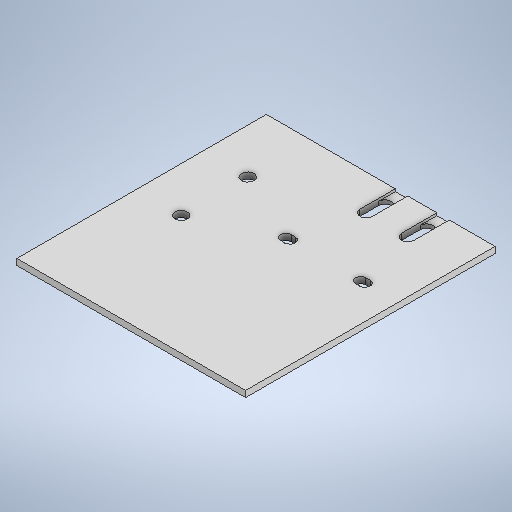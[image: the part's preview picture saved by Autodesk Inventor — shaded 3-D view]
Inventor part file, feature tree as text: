
AUTODESK INVENTOR PART (.ipt)
format: ipt  version: 2025.2 (Build 292293000, 293)  size: 290,816 bytes
history: native  units: mm
features: extrude x5, sketch x4
ambient origin geometry x8: Origin, YZ Plane, XZ Plane, XY Plane, X Axis, Y Axis, Z Axis, Center Point
bodies: Solid1 (feature_tree)
feature tree (9):
  extrude  "Extrusion1"  Depth=120.0mm
  sketch  "Sketch4"  dims[d2=3.0mm d3=0.0mm d14=20.0mm]
  extrude  "Extrusion3"  Depth=20.0mm
  extrude  "Extrusion5"  Depth=6.0mm
  extrude  "Extrusion6"  Depth=5.0mm
  extrude  "Extrusion7"  Depth=5.0mm
  sketch  "Sketch1"  dims[d0=150.0mm d1=120.0mm]
  sketch  "Sketch6"  dims[d15=20.0mm d16=6.0mm]
  sketch  "Sketch7"  dims[d17=6.0mm d18=5.0mm d19=5.0mm d20=3.0mm d21=3.0mm d22=3.0mm d23=3.0mm d24=0.0mm d25=0.0mm d38=1.2mm d39=0.0mm d40=25.0mm d41=43.2mm d42=53.4mm d43=32.0mm d44=6.0mm d45=6.0mm d46=38.0mm d47=5.0mm d48=5.0mm d49=2.0mm d50=2.0mm d51=5.0mm d52=5.0mm d53=0.0mm d54=0.0mm d55=40.0mm d56=0.0mm d57=0.0mm d26=0.5mm d27=0.872665mm d28=0.5mm d29=0.872665mm]
